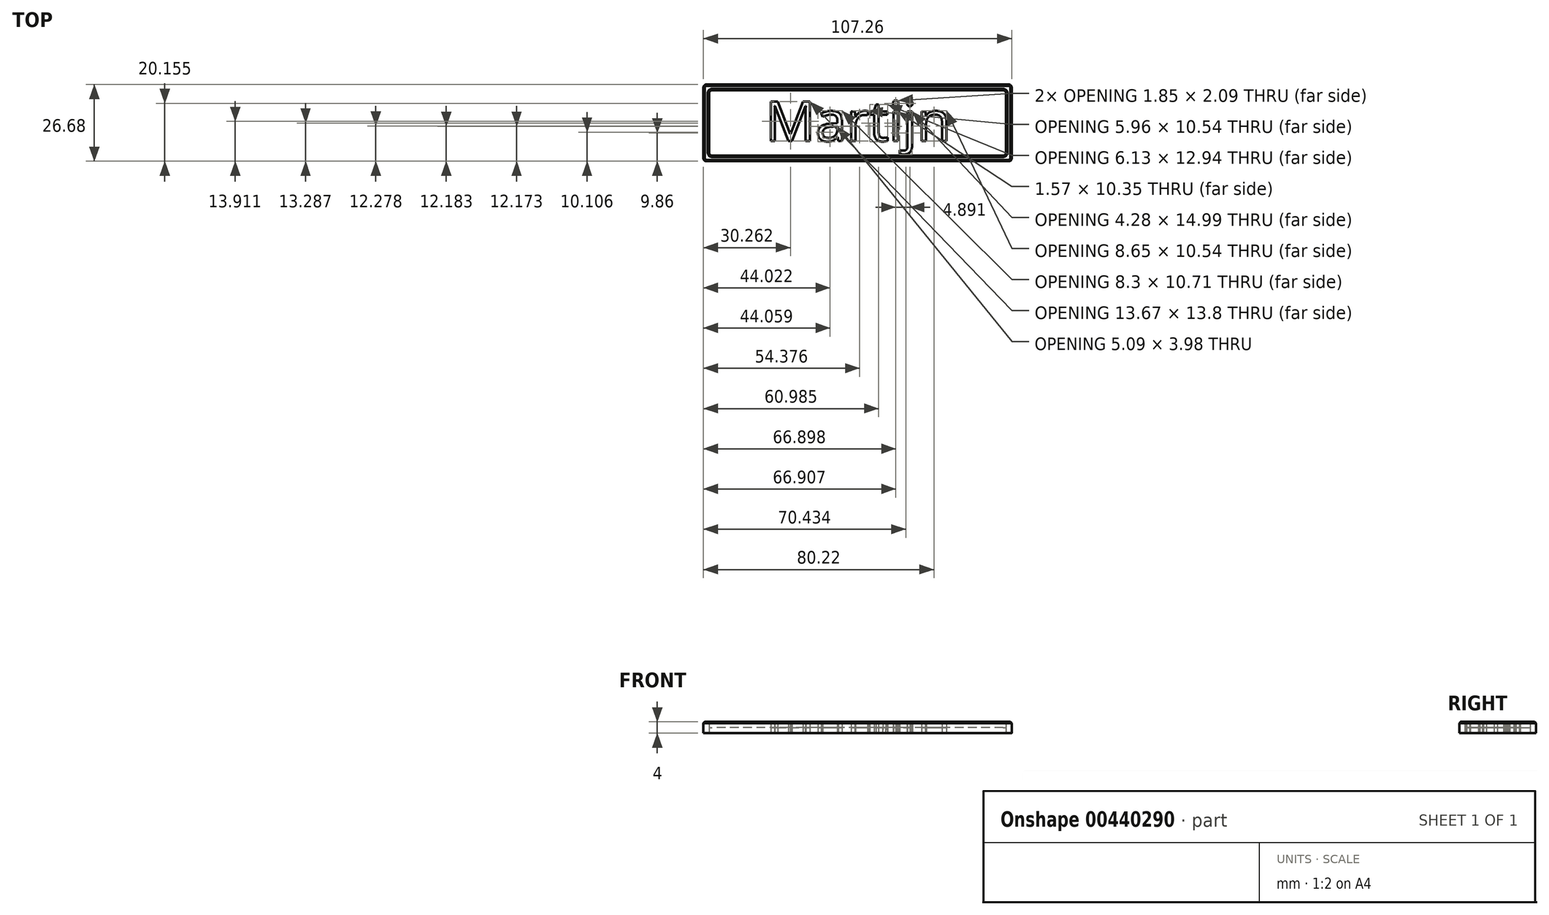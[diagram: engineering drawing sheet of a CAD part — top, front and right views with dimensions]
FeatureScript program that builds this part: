
annotation { "Feature Type Name" : "Feature", "Feature Type Description" : "" }
export const myFeature = defineFeature(function(context is Context, id is Id, definition is map)
    precondition{}
    {
        {
            var Q0;
            Q0=qCreatedBy(makeId("Top.planeOp"),FACE);
            var sketch = newSketch(context, id + "F0", { "sketchPlane" : qUnion([Q0])});
            skLineSegment(sketch, "E0.bottom", {"start": v(52.63, -13.34) * mm, "end": v(-52.63, -13.34) * mm});
            skLineSegment(sketch, "E0.top", {"start": v(52.63, 13.34) * mm, "end": v(-52.63, 13.34) * mm});
            skLineSegment(sketch, "E0.left", {"start": v(53.63, -12.34) * mm, "end": v(53.63, 12.34) * mm});
            skLineSegment(sketch, "E0.right", {"start": v(-53.63, -12.34) * mm, "end": v(-53.63, 12.34) * mm});
            skPoint(sketch, "E0.middle", {"position": v(0, 0) * mm});
            skText(sketch, "E1", { "text": "Martijn", "fontName": "OpenSans-Regular.ttf"});
            skLineSegment(sketch, "E2", {"start": v(-53.63, 13.34) * mm, "end": v(32.2, 13.34) * mm});
            skLineSegment(sketch, "E3.0", {"start": v(50.63, 11.34) * mm, "end": v(-50.63, 11.34) * mm});
            skLineSegment(sketch, "E4.0", {"start": v(51.63, -10.34) * mm, "end": v(51.63, 10.34) * mm});
            skLineSegment(sketch, "E5.0", {"start": v(50.63, -11.34) * mm, "end": v(-50.63, -11.34) * mm});
            skLineSegment(sketch, "E6.0", {"start": v(-51.63, -10.34) * mm, "end": v(-51.63, 10.34) * mm});
            skPoint(sketch, "E7.visualSharp", {"position": v(-53.63, 13.34) * mm});
            skArc(sketch, "E7.filletArc", {"start": v(-52.63, 13.34) * mm, "mid": v(-53.34, 13.05) * mm, "end": v(-53.63, 12.34) * mm});
            skPoint(sketch, "E8.visualSharp", {"position": v(-51.63, 11.34) * mm});
            skArc(sketch, "E8.filletArc", {"start": v(-50.63, 11.34) * mm, "mid": v(-51.34, 11.05) * mm, "end": v(-51.63, 10.34) * mm});
            skPoint(sketch, "E9.visualSharp", {"position": v(-51.63, -11.34) * mm});
            skArc(sketch, "E9.filletArc", {"start": v(-51.63, -10.34) * mm, "mid": v(-51.34, -11.05) * mm, "end": v(-50.63, -11.34) * mm});
            skPoint(sketch, "E10.visualSharp", {"position": v(-53.63, -13.34) * mm});
            skArc(sketch, "E10.filletArc", {"start": v(-53.63, -12.34) * mm, "mid": v(-53.34, -13.05) * mm, "end": v(-52.63, -13.34) * mm});
            skPoint(sketch, "E11.visualSharp", {"position": v(51.63, -11.34) * mm});
            skArc(sketch, "E11.filletArc", {"start": v(50.63, -11.34) * mm, "mid": v(51.34, -11.05) * mm, "end": v(51.63, -10.34) * mm});
            skPoint(sketch, "E12.visualSharp", {"position": v(53.63, -13.34) * mm});
            skArc(sketch, "E12.filletArc", {"start": v(52.63, -13.34) * mm, "mid": v(53.34, -13.05) * mm, "end": v(53.63, -12.34) * mm});
            skPoint(sketch, "E13.visualSharp", {"position": v(53.63, 13.34) * mm});
            skArc(sketch, "E13.filletArc", {"start": v(53.63, 12.34) * mm, "mid": v(53.34, 13.05) * mm, "end": v(52.63, 13.34) * mm});
            skPoint(sketch, "E14.visualSharp", {"position": v(51.63, 11.34) * mm});
            skArc(sketch, "E14.filletArc", {"start": v(51.63, 10.34) * mm, "mid": v(51.34, 11.05) * mm, "end": v(50.63, 11.34) * mm});
            const initialGuessF0  = {"E1": [-0.0321, -0.00633, 1, 0, 0.01392]};
            skSetInitialGuess(sketch, initialGuessF0);
            skSolve(sketch);
        }
        {
            var Q0;
            Q0=makeQuery(id+"F0.imprint","IMPRINT",FACE,{"disambiguationData":[TD([[makeQuery(id+"F0.imprint","IMPRINT",EDGE,{"derivedFrom":sQuery(id+"F0.wireOp",EDGE,"E0.bottom")}),-1.0]])]});
            extrude(context, id + "F1", {"entities" : qUnion([Q0]), "depth" : 4 * mm});
        }
        {
            var Q0;
            Q0=makeQuery(id+"F0.imprint","IMPRINT",FACE,{"disambiguationData":[TD([[makeQuery(id+"F0.imprint","IMPRINT",EDGE,{"derivedFrom":sQuery(id+"F0.wireOp",EDGE,"E1.sketch_text.stroke-106")}),-1.0]])]});
            var Q1;
            Q1=makeQuery(id+"F0.imprint","IMPRINT",FACE,{"disambiguationData":[TD([[makeQuery(id+"F0.imprint","IMPRINT",EDGE,{"derivedFrom":sQuery(id+"F0.wireOp",EDGE,"E1.sketch_text.stroke-89")}),-1.0]])]});
            var Q2;
            Q2=makeQuery(id+"F0.imprint","IMPRINT",FACE,{"disambiguationData":[TD([[makeQuery(id+"F0.imprint","IMPRINT",EDGE,{"derivedFrom":sQuery(id+"F0.wireOp",EDGE,"E1.sketch_text.stroke-98")}),-1.0]])]});
            var Q3;
            Q3=makeQuery(id+"F0.imprint","IMPRINT",FACE,{"disambiguationData":[TD([[makeQuery(id+"F0.imprint","IMPRINT",EDGE,{"derivedFrom":sQuery(id+"F0.wireOp",EDGE,"E1.sketch_text.stroke-77")}),-1.0]])]});
            var Q4;
            Q4=makeQuery(id+"F0.imprint","IMPRINT",FACE,{"disambiguationData":[TD([[makeQuery(id+"F0.imprint","IMPRINT",EDGE,{"derivedFrom":sQuery(id+"F0.wireOp",EDGE,"E1.sketch_text.stroke-81")}),-1.0]])]});
            var Q5;
            Q5=makeQuery(id+"F0.imprint","IMPRINT",FACE,{"disambiguationData":[TD([[makeQuery(id+"F0.imprint","IMPRINT",EDGE,{"derivedFrom":sQuery(id+"F0.wireOp",EDGE,"E1.sketch_text.stroke-58")}),-1.0]])]});
            var Q6;
            Q6=makeQuery(id+"F0.imprint","IMPRINT",FACE,{"disambiguationData":[TD([[makeQuery(id+"F0.imprint","IMPRINT",EDGE,{"derivedFrom":sQuery(id+"F0.wireOp",EDGE,"E1.sketch_text.stroke-45")}),-1.0]])]});
            var Q7;
            Q7=makeQuery(id+"F0.imprint","IMPRINT",FACE,{"disambiguationData":[TD([[makeQuery(id+"F0.imprint","IMPRINT",EDGE,{"derivedFrom":sQuery(id+"F0.wireOp",EDGE,"E1.sketch_text.stroke-18")}),-1.0]])]});
            var Q8;
            Q8=makeQuery(id+"F0.imprint","IMPRINT",FACE,{"disambiguationData":[TD([[makeQuery(id+"F0.imprint","IMPRINT",EDGE,{"derivedFrom":sQuery(id+"F0.wireOp",EDGE,"E1.sketch_text.stroke-0")}),-1.0]])]});
            extrude(context, id + "F2", {"entities" : qUnion([Q0, Q1, Q2, Q3, Q4, Q5, Q6, Q7, Q8]), "depth" : 4 * mm});
        }
        {
            var Q0;
            Q0=makeQuery(id+"F0.imprint","IMPRINT",FACE,{"disambiguationData":[TD([[makeQuery(id+"F0.imprint","IMPRINT",EDGE,{"derivedFrom":sQuery(id+"F0.wireOp",EDGE,"E1.sketch_text.stroke-0")}),1.0]])]});
            var Q1;
            Q1=makeQuery(id+"F0.imprint","IMPRINT",FACE,{"disambiguationData":[TD([[makeQuery(id+"F0.imprint","IMPRINT",EDGE,{"derivedFrom":sQuery(id+"F0.wireOp",EDGE,"E1.sketch_text.stroke-37")}),1.0]])]});
            extrude(context, id + "F3", {"entities" : qUnion([Q0, Q1]), "depth" : 2 * mm});
        }
        {
            var Q0;
            Q0=makeQuery(id+"F1.opExtrude","CAP_EDGE",EDGE,{"disambiguationData":[OSD([sQuery(id+"F0.wireOp",EDGE,"E0.top"),sQuery(id+"F0.wireOp",EDGE,"E2")])],"isStart":false});
            var Q1;
            Q1=makeQuery(id+"F1.opExtrude","CAP_EDGE",EDGE,{"disambiguationData":[OSD([sQuery(id+"F0.wireOp",EDGE,"E7.filletArc")])],"isStart":false});
            var Q2;
            Q2=makeQuery(id+"F1.opExtrude","CAP_EDGE",EDGE,{"disambiguationData":[OSD([sQuery(id+"F0.wireOp",EDGE,"E0.right")])],"isStart":false});
            var Q3;
            Q3=makeQuery(id+"F1.opExtrude","CAP_EDGE",EDGE,{"disambiguationData":[OSD([sQuery(id+"F0.wireOp",EDGE,"E0.bottom")])],"isStart":false});
            var Q4;
            Q4=makeQuery(id+"F1.opExtrude","CAP_EDGE",EDGE,{"disambiguationData":[OSD([sQuery(id+"F0.wireOp",EDGE,"E10.filletArc")])],"isStart":false});
            var Q5;
            Q5=makeQuery(id+"F1.opExtrude","CAP_EDGE",EDGE,{"disambiguationData":[OSD([sQuery(id+"F0.wireOp",EDGE,"E3.0")])],"isStart":false});
            chamfer(context, id + "F4", {"entities" : qUnion([Q0, Q1, Q2, Q3, Q4, Q5]), "width" : 0.5 * mm, "tangentPropagation" : true});
        }
    });
